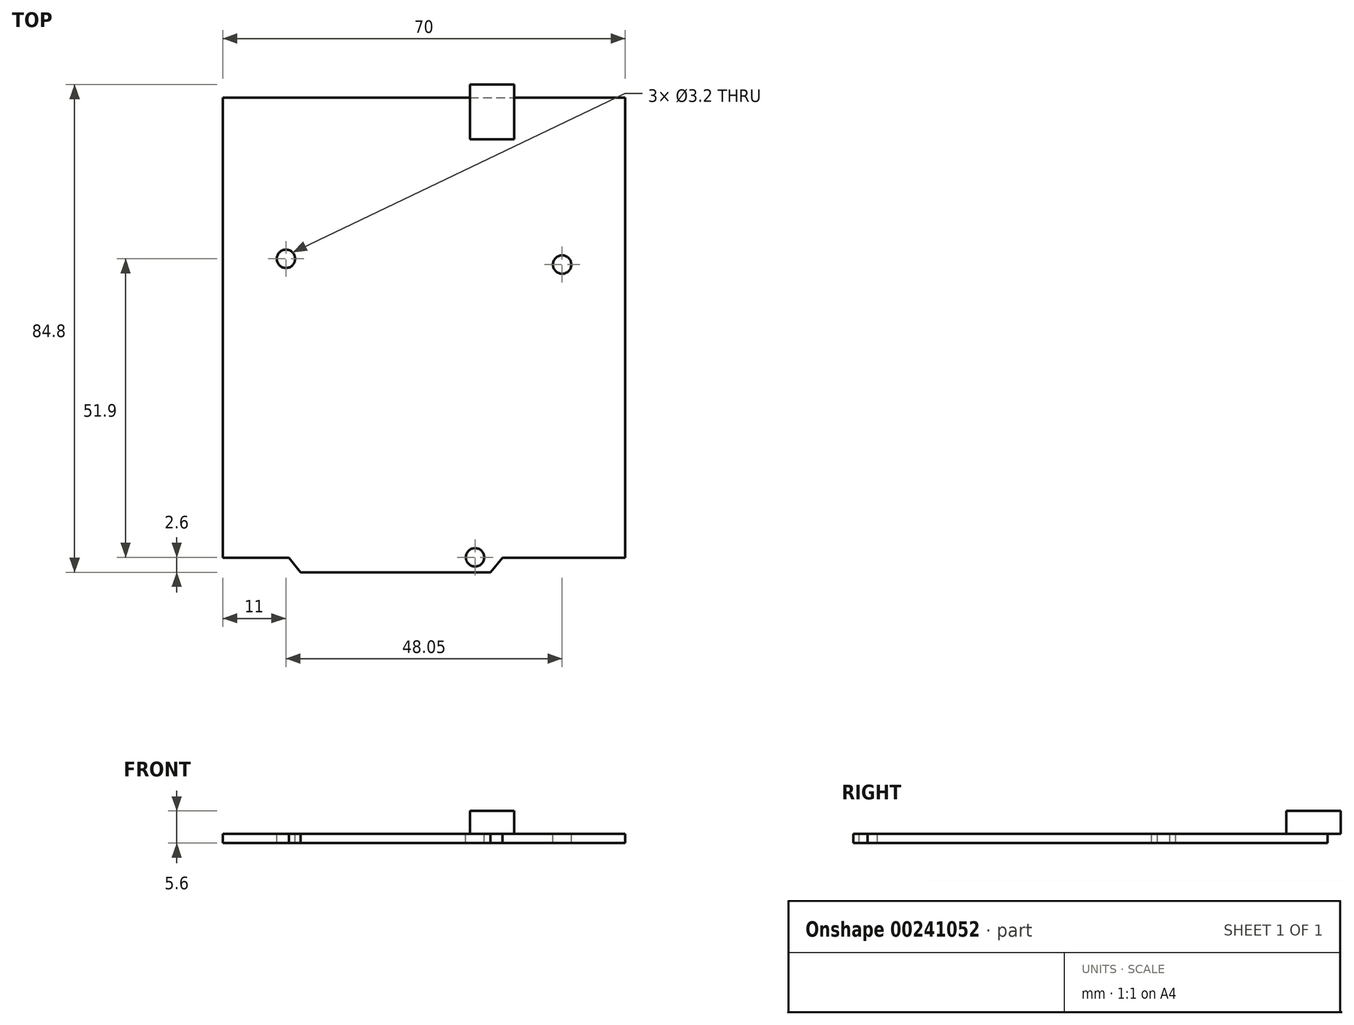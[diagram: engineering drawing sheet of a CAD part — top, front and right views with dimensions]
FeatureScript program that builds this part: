
annotation { "Feature Type Name" : "Feature", "Feature Type Description" : "" }
export const myFeature = defineFeature(function(context is Context, id is Id, definition is map)
    precondition{}
    {
        {
            var Q0;
            Q0=qCreatedBy(makeId("Top.planeOp"),FACE);
            var sketch = newSketch(context, id + "F0", { "sketchPlane" : qUnion([Q0])});
            skLineSegment(sketch, "E0.bottom", {"start": v(-35, 41.25) * mm, "end": v(35, 41.25) * mm});
            skLineSegment(sketch, "E0.top", {"start": v(-35, -41.25) * mm, "end": v(35, -41.25) * mm});
            skLineSegment(sketch, "E0.left", {"start": v(-35, 41.25) * mm, "end": v(-35, -41.25) * mm});
            skLineSegment(sketch, "E0.right", {"start": v(35, 41.25) * mm, "end": v(35, -41.25) * mm});
            skPoint(sketch, "E1", {"position": v(0, 41.25) * mm});
            skPoint(sketch, "E2", {"position": v(35, 0) * mm});
            skLineSegment(sketch, "E3", {"start": v(35, 41.25) * mm, "end": v(35, -38.75) * mm});
            skLineSegment(sketch, "E4", {"start": v(-35, 41.25) * mm, "end": v(-35, -38.75) * mm});
            skLineSegment(sketch, "E5.bottom", {"start": v(-35, -38.75) * mm, "end": v(-23.5, -38.75) * mm});
            skLineSegment(sketch, "E5.top", {"start": v(-35, -41.25) * mm, "end": v(-23.5, -41.25) * mm});
            skLineSegment(sketch, "E5.left", {"start": v(-35, -38.75) * mm, "end": v(-35, -41.25) * mm});
            skLineSegment(sketch, "E5.right", {"start": v(-23.5, -38.75) * mm, "end": v(-23.5, -41.25) * mm});
            skLineSegment(sketch, "E6.bottom", {"start": v(35, -38.75) * mm, "end": v(13.65, -38.75) * mm});
            skLineSegment(sketch, "E6.top", {"start": v(35, -41.25) * mm, "end": v(13.65, -41.25) * mm});
            skLineSegment(sketch, "E6.left", {"start": v(35, -38.75) * mm, "end": v(35, -41.25) * mm});
            skLineSegment(sketch, "E6.right", {"start": v(13.65, -38.75) * mm, "end": v(13.65, -41.25) * mm});
            skLineSegment(sketch, "E7", {"start": v(-21.42, -41.25) * mm, "end": v(11.58, -41.25) * mm});
            skPoint(sketch, "E8", {"position": v(-23.5, -41.25) * mm});
            skPoint(sketch, "E9", {"position": v(-21.42, -41.25) * mm});
            skLineSegment(sketch, "E10", {"start": v(-23.5, -41.25) * mm, "end": v(-21.42, -41.25) * mm});
            skLineSegment(sketch, "E11", {"start": v(11.58, -41.25) * mm, "end": v(13.65, -41.25) * mm});
            skLineSegment(sketch, "E12", {"start": v(-23.5, -38.75) * mm, "end": v(-21.42, -41.25) * mm});
            skLineSegment(sketch, "E13", {"start": v(13.65, -38.75) * mm, "end": v(11.58, -41.25) * mm});
            skLineSegment(sketch, "E14.bottom", {"start": v(-83.2, 38.38) * mm, "end": v(-85.65, 38.38) * mm});
            skSolve(sketch);
        }
        {
            var Q0;
            Q0=makeQuery(id+"F0.imprint","IMPRINT",FACE,{"disambiguationData":[TD([[makeQuery(id+"F0.imprint","IMPRINT",EDGE,{"derivedFrom":sQuery(id+"F0.wireOp",EDGE,"E0.bottom")}),-1.0]])]});
            extrude(context, id + "F1", {"entities" : qUnion([Q0]), "depth" : 1.6 * mm});
        }
        {
            var Q0;
            Q0=makeQuery(id+"F1.opExtrude","CAP_FACE",FACE,{"disambiguationData":[OSD([sQuery(id+"F0.wireOp",EDGE,"E0.bottom"),sQuery(id+"F0.wireOp",EDGE,"E3"),sQuery(id+"F0.wireOp",EDGE,"E4"),sQuery(id+"F0.wireOp",EDGE,"E5.bottom"),sQuery(id+"F0.wireOp",EDGE,"E6.bottom"),sQuery(id+"F0.wireOp",EDGE,"E7"),sQuery(id+"F0.wireOp",EDGE,"E12"),sQuery(id+"F0.wireOp",EDGE,"E13")])],"isStart":false});
            var sketch = newSketch(context, id + "F2", { "sketchPlane" : qUnion([Q0])});
            skCircle(sketch, "E15", {"center": v(8.89, -38.65) * mm, "radius": 1.6 * mm});
            skCircle(sketch, "E16", {"center": v(-24, 13.25) * mm, "radius": 1.6 * mm});
            skCircle(sketch, "E17", {"center": v(24.05, 12.25) * mm, "radius": 1.6 * mm});
            skSolve(sketch);
        }
        {
            var Q0;
            Q0=makeQuery(id+"F2.imprint","IMPRINT",FACE,{"disambiguationData":[TD([[makeQuery(id+"F2.imprint","IMPRINT",EDGE,{"derivedFrom":sQuery(id+"F2.wireOp",EDGE,"E16")}),1.0]])]});
            var Q1;
            Q1=makeQuery(id+"F2.imprint","IMPRINT",FACE,{"disambiguationData":[TD([[makeQuery(id+"F2.imprint","IMPRINT",EDGE,{"derivedFrom":sQuery(id+"F2.wireOp",EDGE,"E17")}),1.0]])]});
            var Q2;
            Q2=makeQuery(id+"F2.imprint","IMPRINT",FACE,{"disambiguationData":[TD([[makeQuery(id+"F2.imprint","IMPRINT",EDGE,{"derivedFrom":sQuery(id+"F2.wireOp",EDGE,"E15")}),1.0]])]});
            extrude(context, id + "F3", {"entities" : qUnion([Q0, Q1, Q2]), "operationType" : NewBodyOperationType.REMOVE, "endBound" : BoundingType.UP_TO_NEXT, "oppositeDirection" : true, "depth" : 25 * mm});
        }
        {
            var Q0;
            Q0=makeQuery(id+"F1.opExtrude","CAP_FACE",FACE,{"disambiguationData":[OSD([sQuery(id+"F0.wireOp",EDGE,"E0.bottom"),sQuery(id+"F0.wireOp",EDGE,"E3"),sQuery(id+"F0.wireOp",EDGE,"E4"),sQuery(id+"F0.wireOp",EDGE,"E5.bottom"),sQuery(id+"F0.wireOp",EDGE,"E6.bottom"),sQuery(id+"F0.wireOp",EDGE,"E7"),sQuery(id+"F0.wireOp",EDGE,"E12"),sQuery(id+"F0.wireOp",EDGE,"E13")])],"isStart":false});
            var sketch = newSketch(context, id + "F4", { "sketchPlane" : qUnion([Q0])});
            skLineSegment(sketch, "E18.bottom", {"start": v(8, 43.55) * mm, "end": v(15.7, 43.55) * mm});
            skLineSegment(sketch, "E18.top", {"start": v(8, 34.05) * mm, "end": v(15.7, 34.05) * mm});
            skLineSegment(sketch, "E18.left", {"start": v(8, 43.55) * mm, "end": v(8, 34.05) * mm});
            skLineSegment(sketch, "E18.right", {"start": v(15.7, 43.55) * mm, "end": v(15.7, 34.05) * mm});
            skSolve(sketch);
        }
        {
            var Q0;
            {var subQ0=sQuery(id+"F4.wireOp",EDGE,"E18.bottom");Q0=makeQuery(id+"F4.imprint","IMPRINT",FACE,{"disambiguationData":[TD([[makeQuery(id+"F4.imprint","IMPRINT",EDGE,{"derivedFrom":subQ0}),-1.0]])]});}
            var Q1;
            {var subQ0=sQuery(id+"F4.wireOp",EDGE,"E18.top");Q1=makeQuery(id+"F4.imprint","IMPRINT",FACE,{"disambiguationData":[TD([[makeQuery(id+"F4.imprint","IMPRINT",EDGE,{"derivedFrom":subQ0}),1.0]])]});}
            var Q2;
            Q2=sQuery(id+"F4.wireOp",EDGE,"E18.left");
            var Q3;
            Q3=sQuery(id+"F4.wireOp",EDGE,"E18.bottom");
            var Q4;
            Q4=sQuery(id+"F4.wireOp",EDGE,"E18.right");
            var Q5;
            Q5=sQuery(id+"F4.wireOp",EDGE,"E18.top");
            extrude(context, id + "F5", {"entities" : qUnion([Q0, Q1]), "surfaceEntities" : qUnion([Q2, Q3, Q4, Q5]), "depth" : 4 * mm});
        }
    });
